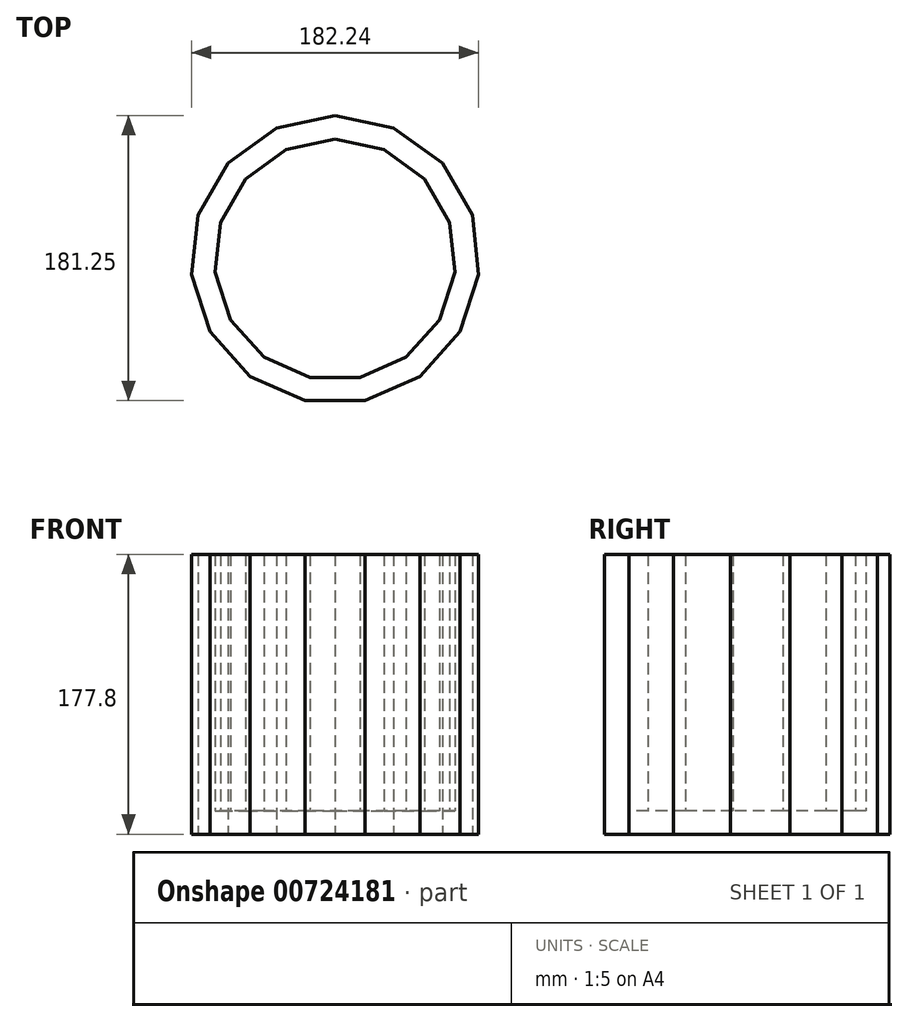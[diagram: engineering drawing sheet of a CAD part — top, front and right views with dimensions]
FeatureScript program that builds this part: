
annotation { "Feature Type Name" : "Feature", "Feature Type Description" : "" }
export const myFeature = defineFeature(function(context is Context, id is Id, definition is map)
    precondition{}
    {
        {
            var Q0;
            Q0=qCreatedBy(makeId("Top.planeOp"),FACE);
            var sketch = newSketch(context, id + "F0", { "sketchPlane" : qUnion([Q0])});
            skCircle(sketch, "E0.cCircle", {"center": v(0, 0) * mm, "radius": 89.62 * mm, "construction": true});
            skLineSegment(sketch, "E0.0", {"start": v(19.05, -89.62) * mm, "end": v(-19.05, -89.62) * mm});
            skLineSegment(sketch, "E0.1", {"start": v(-19.05, -89.62) * mm, "end": v(-53.86, -74.13) * mm});
            skLineSegment(sketch, "E0.2", {"start": v(-53.86, -74.13) * mm, "end": v(-79.35, -45.81) * mm});
            skLineSegment(sketch, "E0.3", {"start": v(-79.35, -45.81) * mm, "end": v(-91.12, -9.58) * mm});
            skLineSegment(sketch, "E0.4", {"start": v(-91.12, -9.58) * mm, "end": v(-87.14, 28.31) * mm});
            skLineSegment(sketch, "E0.5", {"start": v(-87.14, 28.31) * mm, "end": v(-68.1, 61.3) * mm});
            skLineSegment(sketch, "E0.6", {"start": v(-68.1, 61.3) * mm, "end": v(-37.27, 83.7) * mm});
            skLineSegment(sketch, "E0.7", {"start": v(-37.27, 83.7) * mm, "end": v(0, 91.63) * mm});
            skLineSegment(sketch, "E0.8", {"start": v(0, 91.63) * mm, "end": v(37.27, 83.7) * mm});
            skLineSegment(sketch, "E0.9", {"start": v(37.27, 83.7) * mm, "end": v(68.1, 61.3) * mm});
            skLineSegment(sketch, "E0.10", {"start": v(68.1, 61.3) * mm, "end": v(87.14, 28.31) * mm});
            skLineSegment(sketch, "E0.11", {"start": v(87.14, 28.31) * mm, "end": v(91.12, -9.58) * mm});
            skLineSegment(sketch, "E0.12", {"start": v(91.12, -9.58) * mm, "end": v(79.35, -45.81) * mm});
            skLineSegment(sketch, "E0.13", {"start": v(79.35, -45.81) * mm, "end": v(53.86, -74.13) * mm});
            skLineSegment(sketch, "E0.14", {"start": v(53.86, -74.13) * mm, "end": v(19.05, -89.62) * mm});
            skPoint(sketch, "E0.0.midPoint", {"position": v(0, -89.62) * mm});
            skSolve(sketch);
        }
        {
            var Q0;
            Q0=makeQuery(id+"F0.imprint","IMPRINT",FACE,{"disambiguationData":[TD([[makeQuery(id+"F0.imprint","IMPRINT",EDGE,{"derivedFrom":sQuery(id+"F0.wireOp",EDGE,"E0.0")}),-1.0]])]});
            extrude(context, id + "F1", {"entities" : qUnion([Q0]), "depth" : 177.8 * mm, "offsetDistance" : 25.4 * mm});
        }
        {
            var Q0;
            Q0=makeQuery(id+"F1.opExtrude","CAP_FACE",FACE,{"disambiguationData":[OSD([sQuery(id+"F0.wireOp",EDGE,"E0.0"),sQuery(id+"F0.wireOp",EDGE,"E0.1"),sQuery(id+"F0.wireOp",EDGE,"E0.2"),sQuery(id+"F0.wireOp",EDGE,"E0.3"),sQuery(id+"F0.wireOp",EDGE,"E0.4"),sQuery(id+"F0.wireOp",EDGE,"E0.5"),sQuery(id+"F0.wireOp",EDGE,"E0.6"),sQuery(id+"F0.wireOp",EDGE,"E0.7"),sQuery(id+"F0.wireOp",EDGE,"E0.8"),sQuery(id+"F0.wireOp",EDGE,"E0.9"),sQuery(id+"F0.wireOp",EDGE,"E0.10"),sQuery(id+"F0.wireOp",EDGE,"E0.11"),sQuery(id+"F0.wireOp",EDGE,"E0.12"),sQuery(id+"F0.wireOp",EDGE,"E0.13"),sQuery(id+"F0.wireOp",EDGE,"E0.14")])],"isStart":false});
            shell(context, id + "F2", {"entities" : qUnion([Q0]), "thickness" : 14.82 * mm});
        }
    });
